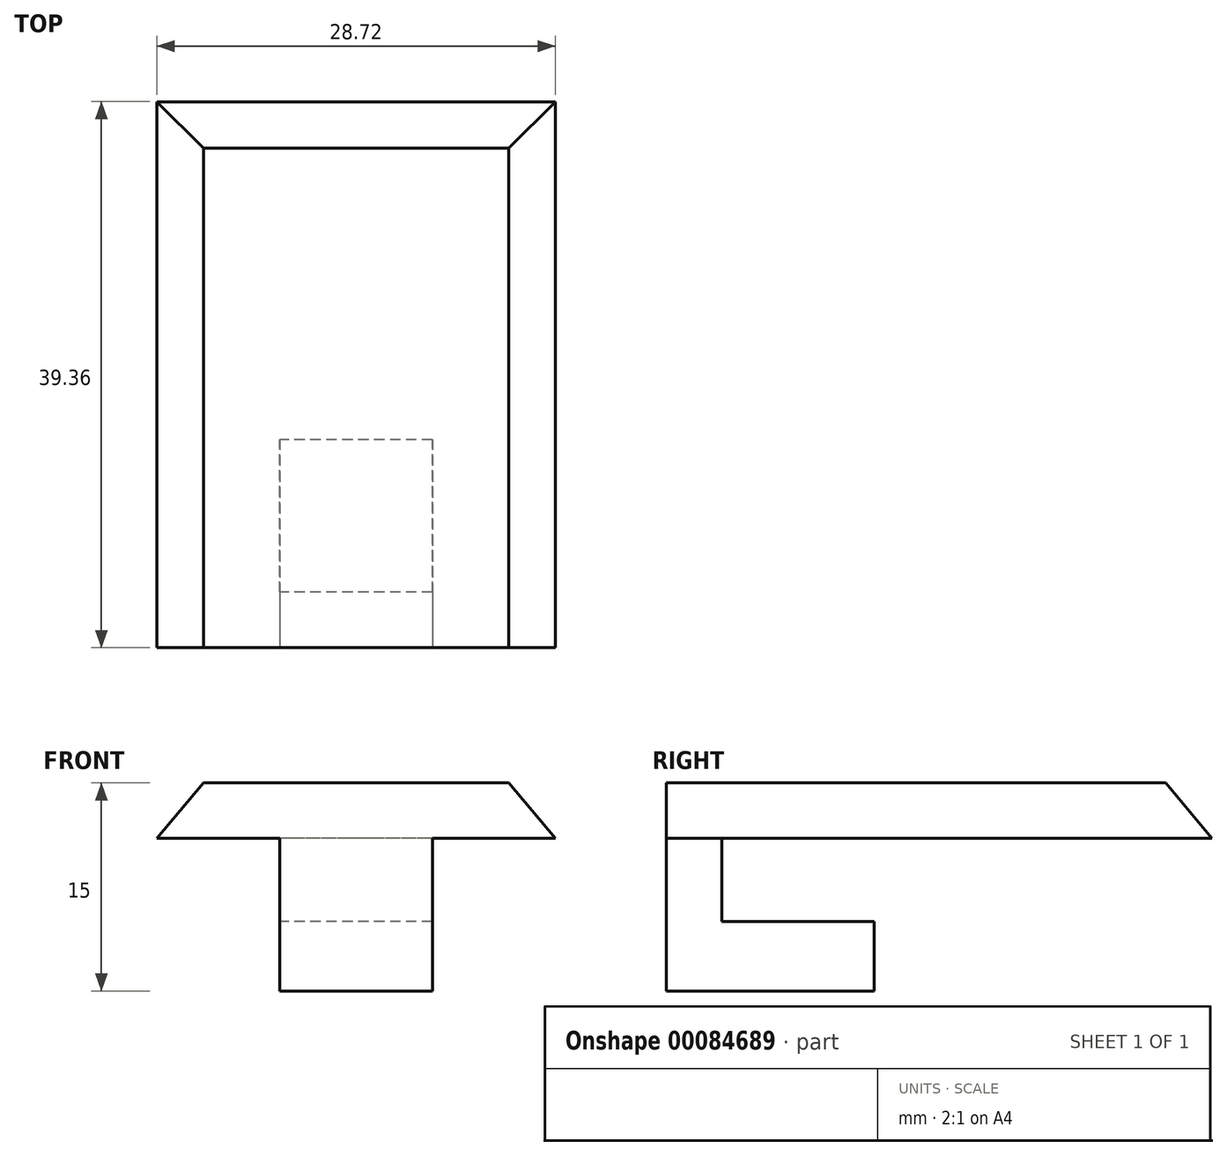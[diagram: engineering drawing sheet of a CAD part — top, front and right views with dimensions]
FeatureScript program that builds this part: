
annotation { "Feature Type Name" : "Feature", "Feature Type Description" : "" }
export const myFeature = defineFeature(function(context is Context, id is Id, definition is map)
    precondition{}
    {
        {
            var Q0;
            Q0=qCreatedBy(makeId("Right.planeOp"),FACE);
            var sketch = newSketch(context, id + "F0", { "sketchPlane" : qUnion([Q0])});
            skLineSegment(sketch, "E0", {"start": v(0, 0) * mm, "end": v(-11, 0) * mm});
            skLineSegment(sketch, "E1", {"start": v(-11, 5) * mm, "end": v(0, 5) * mm});
            skLineSegment(sketch, "E2", {"start": v(0, 5) * mm, "end": v(0, 0) * mm});
            skLineSegment(sketch, "E3", {"start": v(-15, 0) * mm, "end": v(-15, 15) * mm});
            skLineSegment(sketch, "E4", {"start": v(-15, 15) * mm, "end": v(25, 15) * mm});
            skLineSegment(sketch, "E5", {"start": v(25, 15) * mm, "end": v(25, 11) * mm});
            skLineSegment(sketch, "E6", {"start": v(25, 11) * mm, "end": v(-11, 11) * mm});
            skLineSegment(sketch, "E7", {"start": v(-11, 11) * mm, "end": v(-11, 5) * mm});
            skLineSegment(sketch, "E8", {"start": v(-11, 0) * mm, "end": v(-15, 0) * mm});
            skLineSegment(sketch, "E9", {"start": v(-11, 11) * mm, "end": v(-15, 11) * mm});
            skSolve(sketch);
        }
        {
            var Q0;
            Q0=makeQuery(id+"F0.imprint","IMPRINT",FACE,{"disambiguationData":[TD([[makeQuery(id+"F0.imprint","IMPRINT",EDGE,{"derivedFrom":sQuery(id+"F0.wireOp",EDGE,"E0")}),-1.0]])]});
            extrude(context, id + "F1", {"entities" : qUnion([Q0]), "endBound" : BoundingType.SYMMETRIC, "depth" : 11 * mm});
        }
        {
            var Q0;
            {var subQ0=sQuery(id+"F0.wireOp",EDGE,"E4");Q0=makeQuery(id+"F0.imprint","IMPRINT",FACE,{"disambiguationData":[TD([[makeQuery(id+"F0.imprint","IMPRINT",EDGE,{"derivedFrom":subQ0}),-1.0]])]});}
            extrude(context, id + "F2", {"entities" : qUnion([Q0]), "operationType" : NewBodyOperationType.ADD, "endBound" : BoundingType.SYMMETRIC, "depth" : 30 * mm});
        }
        {
            var Q0;
            Q0=makeQuery(id+"F2.opExtrude","CAP_EDGE",EDGE,{"disambiguationData":[OSD([sQuery(id+"F0.wireOp",EDGE,"E4")])],"isStart":false});
            var Q1;
            Q1=makeQuery(id+"F2.opExtrude","SWEPT_EDGE",EDGE,{"disambiguationData":[OSD([sQuery(id+"F0.wireOp",EDGE,"E4"),sQuery(id+"F0.wireOp",EDGE,"E5")])]});
            var Q2;
            Q2=makeQuery(id+"F2.opExtrude","CAP_EDGE",EDGE,{"disambiguationData":[OSD([sQuery(id+"F0.wireOp",EDGE,"E4")])],"isStart":true});
            chamfer(context, id + "F3", {"entities" : qUnion([Q0, Q1, Q2]), "chamferType" : ChamferType.OFFSET_ANGLE, "width" : 4 * mm, "oppositeDirection" : false, "angle" : 50 * degree, "tangentPropagation" : true});
        }
    });
